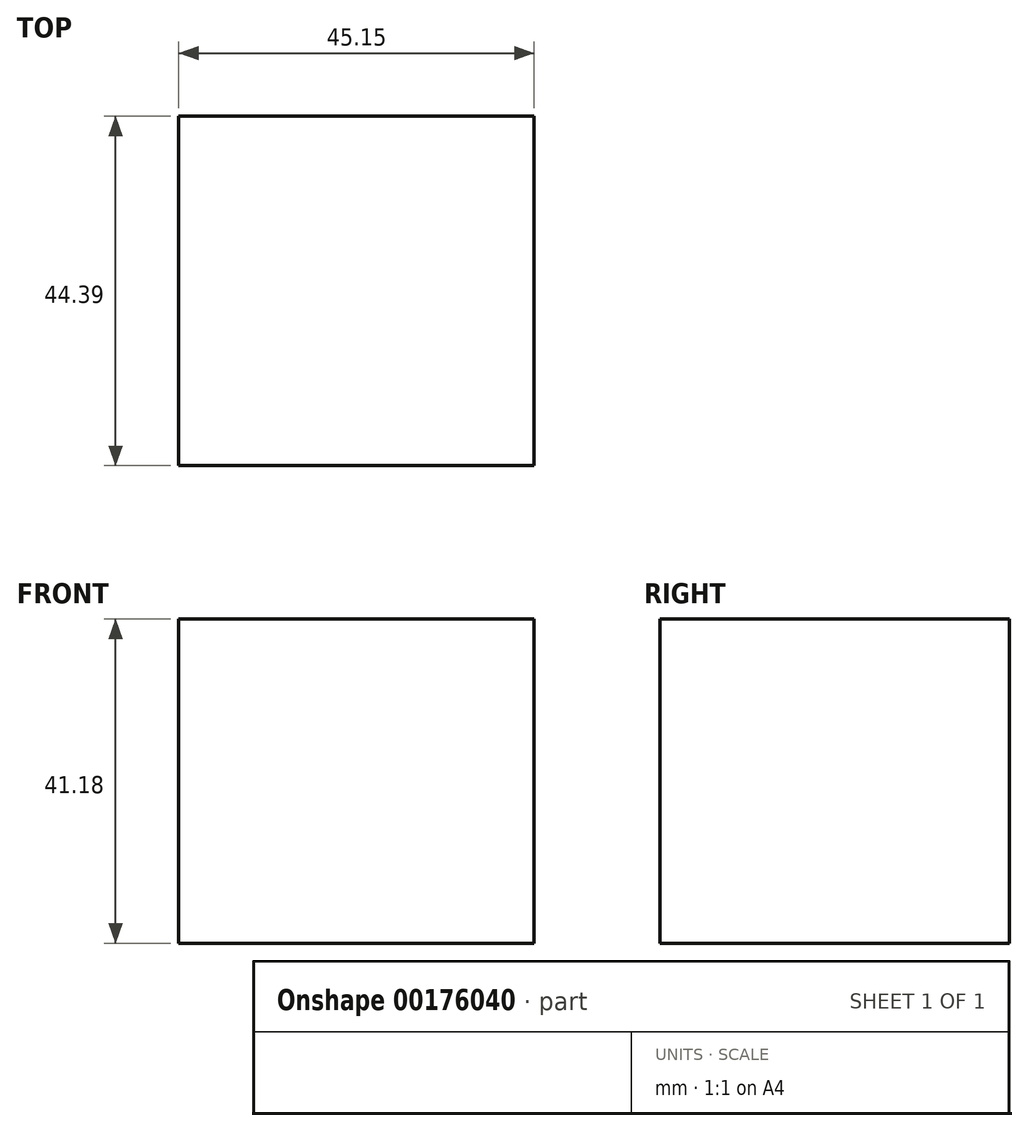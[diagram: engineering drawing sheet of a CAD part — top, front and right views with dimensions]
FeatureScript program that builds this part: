
annotation { "Feature Type Name" : "Feature", "Feature Type Description" : "" }
export const myFeature = defineFeature(function(context is Context, id is Id, definition is map)
    precondition{}
    {
        {
            var Q0;
            Q0=qCreatedBy(makeId("Front.planeOp"),FACE);
            var sketch = newSketch(context, id + "F0", { "sketchPlane" : qUnion([Q0])});
            skLineSegment(sketch, "E0", {"start": v(0, 41.18) * mm, "end": v(-45.15, 41.18) * mm});
            skLineSegment(sketch, "E1", {"start": v(-45.15, 41.18) * mm, "end": v(-45.15, 0) * mm});
            skLineSegment(sketch, "E2", {"start": v(-45.15, 0) * mm, "end": v(0, 0) * mm});
            skLineSegment(sketch, "E3", {"start": v(0, 0) * mm, "end": v(0, 41.18) * mm});
            skSolve(sketch);
        }
        {
            var Q0;
            Q0 = qSketchRegion(id + "F0", true);
            extrude(context, id + "F1", {"entities" : qUnion([Q0]), "depth" : 44.4 * mm});
        }
    });
